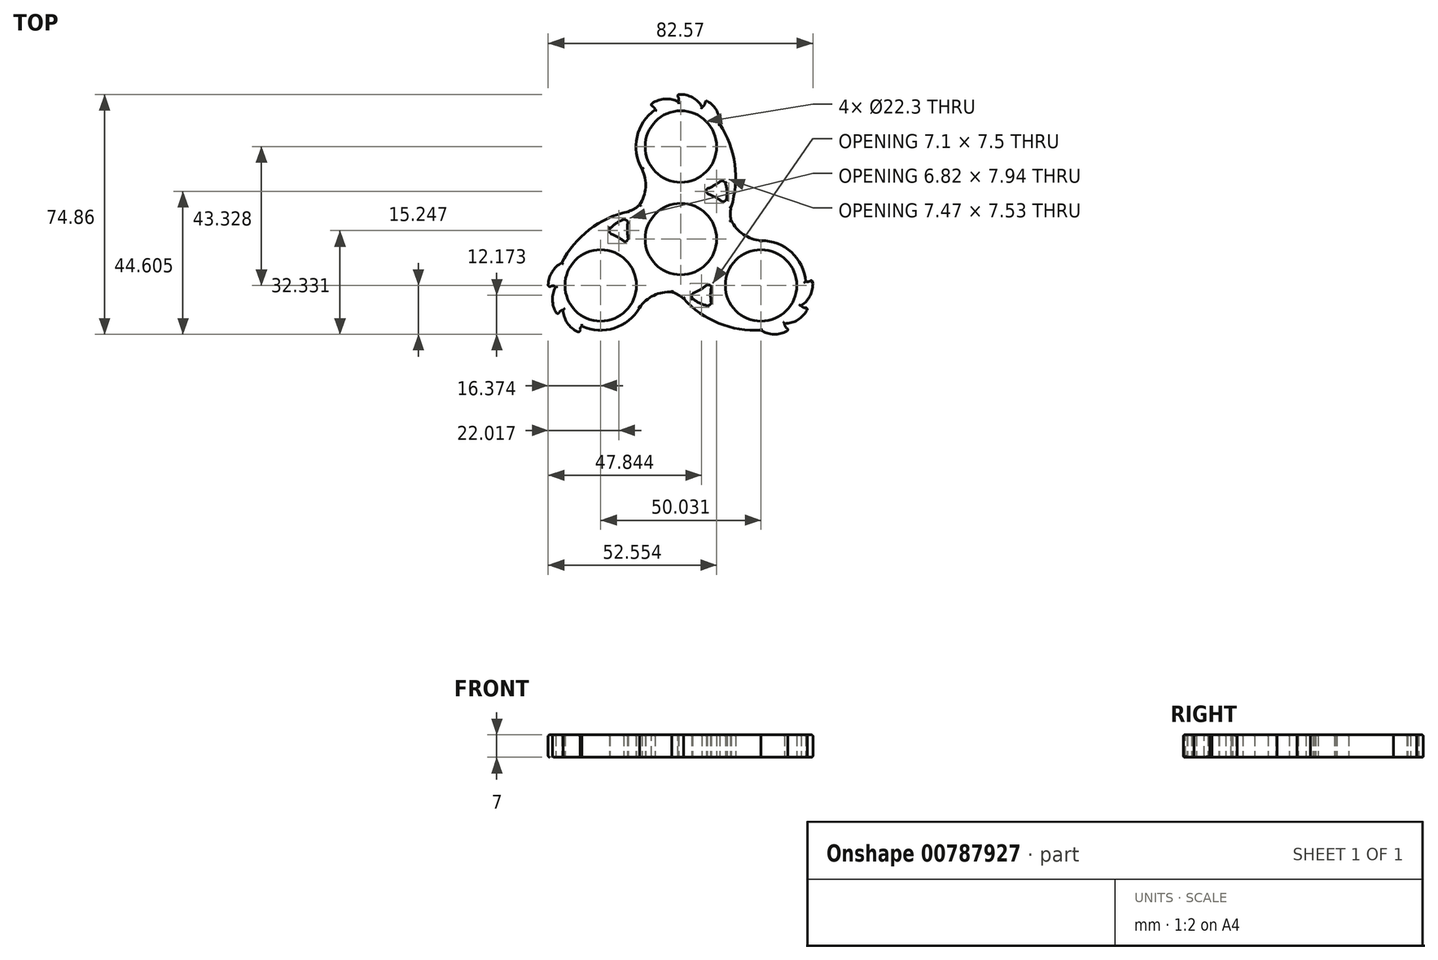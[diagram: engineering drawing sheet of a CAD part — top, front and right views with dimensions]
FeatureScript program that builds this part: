
annotation { "Feature Type Name" : "Feature", "Feature Type Description" : "" }
export const myFeature = defineFeature(function(context is Context, id is Id, definition is map)
    precondition{}
    {
        {
            var Q0;
            Q0=qCreatedBy(makeId("Top.planeOp"),FACE);
            var sketch = newSketch(context, id + "F0", { "sketchPlane" : qUnion([Q0])});
            skCircle(sketch, "E0", {"center": v(0, 28.89) * mm, "radius": 11.15 * mm});
            skCircle(sketch, "E1", {"center": v(0, 0) * mm, "radius": 14 * mm});
            skPoint(sketch, "E2.center", {"position": v(-0.02, -0.02) * mm});
            skPoint(sketch, "E3.1.3", {"position": v(0.02, 0) * mm});
            skPoint(sketch, "E3.2.3", {"position": v(0, 0.02) * mm});
            skArc(sketch, "E4", {"start": v(15.68, 10) * mm, "mid": v(16.82, 23.32) * mm, "end": v(12.15, 35.85) * mm});
            skArc(sketch, "E5", {"start": v(8.03, 15.65) * mm, "mid": v(7.97, 14.84) * mm, "end": v(8.4, 14.15) * mm});
            skArc(sketch, "E6", {"start": v(15.68, 10) * mm, "mid": v(15.44, 7.9) * mm, "end": v(15.68, 5.81) * mm});
            skArc(sketch, "E7", {"start": v(15.68, 5.81) * mm, "mid": v(19.88, 1.21) * mm, "end": v(25.87, -0.48) * mm});
            skArc(sketch, "E8", {"start": v(12.15, 35.85) * mm, "mid": v(10.91, 40.47) * mm, "end": v(7.24, 43.54) * mm});
            skArc(sketch, "E9", {"start": v(6.62, 41.22) * mm, "mid": v(7.48, 42.23) * mm, "end": v(7.24, 43.54) * mm});
            skArc(sketch, "E10", {"start": v(6.62, 41.22) * mm, "mid": v(3.06, 44.45) * mm, "end": v(-1.72, 45.02) * mm});
            skArc(sketch, "E11", {"start": v(-0.79, 42.86) * mm, "mid": v(-0.75, 44.16) * mm, "end": v(-1.72, 45.02) * mm});
            skArc(sketch, "E12", {"start": v(-0.79, 42.86) * mm, "mid": v(-5.54, 43.68) * mm, "end": v(-9.88, 41.6) * mm});
            skArc(sketch, "E13", {"start": v(-8.04, 40.35) * mm, "mid": v(-8.7, 41.36) * mm, "end": v(-9.88, 41.6) * mm});
            skArc(sketch, "E14", {"start": v(13.9, 17.47) * mm, "mid": v(13.31, 18.04) * mm, "end": v(12.5, 18.16) * mm});
            skArc(sketch, "E15", {"start": v(12.86, 11.66) * mm, "mid": v(13.65, 11.81) * mm, "end": v(14.21, 12.4) * mm});
            skArc(sketch, "E16", {"start": v(12.86, 11.66) * mm, "mid": v(10.72, 13.08) * mm, "end": v(8.4, 14.15) * mm});
            skArc(sketch, "E17", {"start": v(14.21, 12.4) * mm, "mid": v(14.38, 14.96) * mm, "end": v(13.9, 17.47) * mm});
            skArc(sketch, "E18", {"start": v(8.03, 15.65) * mm, "mid": v(10.38, 16.71) * mm, "end": v(12.5, 18.16) * mm});
            skArc(sketch, "E19.1.0", {"start": v(-12.88, 10.68) * mm, "mid": v(-10.99, 16.61) * mm, "end": v(-12.52, 22.64) * mm});
            skCircle(sketch, "E20", {"center": v(0, 0) * mm, "radius": 11.15 * mm});
            skCircle(sketch, "E21", {"center": v(0, 28.89) * mm, "radius": 14 * mm});
            skArc(sketch, "E22.1.0", {"start": v(-16.53, 5.3) * mm, "mid": v(-16.69, 2.75) * mm, "end": v(-16.45, 0.2) * mm});
            skArc(sketch, "E22.1.1", {"start": v(-17.85, 6.1) * mm, "mid": v(-20.15, 4.97) * mm, "end": v(-22.08, 3.3) * mm});
            skArc(sketch, "E22.1.2", {"start": v(-16.5, 8.59) * mm, "mid": v(-28.6, 2.9) * mm, "end": v(-37.12, -7.4) * mm});
            skArc(sketch, "E22.1.3", {"start": v(-37.12, -7.4) * mm, "mid": v(-40.5, -10.78) * mm, "end": v(-41.32, -15.5) * mm});
            skCircle(sketch, "E22.1.5", {"center": v(-25.02, -14.44) * mm, "radius": 11.15 * mm});
            skArc(sketch, "E22.1.7", {"start": v(-16.5, 8.59) * mm, "mid": v(-14.57, 9.42) * mm, "end": v(-12.88, 10.68) * mm});
            skArc(sketch, "E22.1.8", {"start": v(-39, -14.87) * mm, "mid": v(-40.03, -19.58) * mm, "end": v(-38.13, -24) * mm});
            skArc(sketch, "E22.1.9", {"start": v(-17.57, -0.87) * mm, "mid": v(-19.66, 0.63) * mm, "end": v(-21.98, 1.75) * mm});
            skCircle(sketch, "E22.1.10", {"center": v(-25.02, -14.44) * mm, "radius": 14 * mm});
            skArc(sketch, "E22.1.12", {"start": v(-36.73, -22.11) * mm, "mid": v(-35.06, -26.64) * mm, "end": v(-31.08, -29.36) * mm});
            skArc(sketch, "E22.1.13", {"start": v(-2.8, -16.49) * mm, "mid": v(-8.9, -17.82) * mm, "end": v(-13.35, -22.17) * mm});
            skArc(sketch, "E22.1.15", {"start": v(-30.92, -27.14) * mm, "mid": v(-31.48, -28.21) * mm, "end": v(-31.08, -29.36) * mm});
            skArc(sketch, "E22.1.18", {"start": v(-16.53, 5.3) * mm, "mid": v(-17.06, 5.92) * mm, "end": v(-17.85, 6.1) * mm});
            skArc(sketch, "E22.1.19", {"start": v(-39, -14.87) * mm, "mid": v(-40.31, -14.63) * mm, "end": v(-41.32, -15.5) * mm});
            skArc(sketch, "E22.1.20", {"start": v(-36.73, -22.11) * mm, "mid": v(-37.87, -22.73) * mm, "end": v(-38.13, -24) * mm});
            skArc(sketch, "E22.1.21", {"start": v(-17.57, -0.87) * mm, "mid": v(-16.84, -0.52) * mm, "end": v(-16.45, 0.2) * mm});
            skArc(sketch, "E22.1.22", {"start": v(-22.08, 3.3) * mm, "mid": v(-22.28, 2.5) * mm, "end": v(-21.98, 1.75) * mm});
            skArc(sketch, "E22.2.0", {"start": v(3.67, -16.96) * mm, "mid": v(5.97, -15.82) * mm, "end": v(8.06, -14.35) * mm});
            skArc(sketch, "E22.2.1", {"start": v(3.64, -18.5) * mm, "mid": v(5.77, -19.93) * mm, "end": v(8.19, -20.77) * mm});
            skArc(sketch, "E22.2.2", {"start": v(0.81, -18.58) * mm, "mid": v(11.78, -26.23) * mm, "end": v(24.97, -28.44) * mm});
            skArc(sketch, "E22.2.3", {"start": v(24.97, -28.44) * mm, "mid": v(29.59, -29.69) * mm, "end": v(34.08, -28.04) * mm});
            skCircle(sketch, "E22.2.5", {"center": v(25.02, -14.44) * mm, "radius": 11.15 * mm});
            skArc(sketch, "E22.2.6", {"start": v(-2.8, -16.49) * mm, "mid": v(-8.9, -17.82) * mm, "end": v(-13.35, -22.17) * mm});
            skArc(sketch, "E22.2.7", {"start": v(0.81, -18.58) * mm, "mid": v(-0.88, -17.33) * mm, "end": v(-2.8, -16.49) * mm});
            skArc(sketch, "E22.2.8", {"start": v(32.39, -26.35) * mm, "mid": v(36.97, -24.88) * mm, "end": v(39.85, -21.02) * mm});
            skArc(sketch, "E22.2.9", {"start": v(9.54, -14.78) * mm, "mid": v(9.29, -17.34) * mm, "end": v(9.47, -19.91) * mm});
            skCircle(sketch, "E22.2.10", {"center": v(25.02, -14.44) * mm, "radius": 14 * mm});
            skArc(sketch, "E22.2.12", {"start": v(37.51, -20.75) * mm, "mid": v(40.6, -17.05) * mm, "end": v(40.96, -12.24) * mm});
            skArc(sketch, "E22.2.15", {"start": v(38.96, -13.21) * mm, "mid": v(40.17, -13.15) * mm, "end": v(40.96, -12.24) * mm});
            skArc(sketch, "E22.2.18", {"start": v(3.67, -16.96) * mm, "mid": v(3.4, -17.73) * mm, "end": v(3.64, -18.5) * mm});
            skArc(sketch, "E22.2.19", {"start": v(32.39, -26.35) * mm, "mid": v(32.83, -27.6) * mm, "end": v(34.08, -28.04) * mm});
            skArc(sketch, "E22.2.20", {"start": v(37.51, -20.75) * mm, "mid": v(38.62, -21.43) * mm, "end": v(39.85, -21.02) * mm});
            skArc(sketch, "E22.2.21", {"start": v(9.54, -14.78) * mm, "mid": v(8.87, -14.32) * mm, "end": v(8.06, -14.35) * mm});
            skArc(sketch, "E22.2.22", {"start": v(8.19, -20.77) * mm, "mid": v(8.97, -20.55) * mm, "end": v(9.47, -19.91) * mm});
            skSolve(sketch);
        }
        {
            var Q0;
            {var subQ12=sQuery(id+"F0.wireOp",EDGE,"E4");Q0=makeQuery(id+"F0.imprint","IMPRINT",FACE,{"disambiguationData":[TD([[makeQuery(id+"F0.imprint","IMPRINT",EDGE,{"derivedFrom":subQ12}),1.0]])]});}
            var Q1;
            Q1=makeQuery(id+"F0.imprint","IMPRINT",FACE,{"disambiguationData":[TD([[makeQuery(id+"F0.imprint","IMPRINT",EDGE,{"derivedFrom":sQuery(id+"F0.wireOp",EDGE,"E0")}),-1.0]])]});
            var Q2;
            Q2=makeQuery(id+"F0.imprint","IMPRINT",FACE,{"disambiguationData":[TD([[makeQuery(id+"F0.imprint","IMPRINT",EDGE,{"derivedFrom":sQuery(id+"F0.wireOp",EDGE,"E22.1.5")}),-1.0]])]});
            var Q3;
            Q3=makeQuery(id+"F0.imprint","IMPRINT",FACE,{"disambiguationData":[TD([[makeQuery(id+"F0.imprint","IMPRINT",EDGE,{"derivedFrom":sQuery(id+"F0.wireOp",EDGE,"E22.2.5")}),-1.0]])]});
            var Q4;
            Q4=makeQuery(id+"F0.imprint","IMPRINT",FACE,{"disambiguationData":[TD([[makeQuery(id+"F0.imprint","IMPRINT",EDGE,{"derivedFrom":sQuery(id+"F0.wireOp",EDGE,"E1")}),1.0]])]});
            var Q5;
            {var subQ0=sQuery(id+"F0.wireOp",EDGE,"E12");Q5=makeQuery(id+"F0.imprint","IMPRINT",FACE,{"disambiguationData":[TD([[makeQuery(id+"F0.imprint","IMPRINT",EDGE,{"derivedFrom":subQ0}),1.0]])]});}
            var Q6;
            {var subQ0=sQuery(id+"F0.wireOp",EDGE,"E10");Q6=makeQuery(id+"F0.imprint","IMPRINT",FACE,{"disambiguationData":[TD([[makeQuery(id+"F0.imprint","IMPRINT",EDGE,{"derivedFrom":subQ0}),1.0]])]});}
            var Q7;
            {var subQ0=sQuery(id+"F0.wireOp",EDGE,"E8");Q7=makeQuery(id+"F0.imprint","IMPRINT",FACE,{"disambiguationData":[TD([[makeQuery(id+"F0.imprint","IMPRINT",EDGE,{"derivedFrom":subQ0}),1.0]])]});}
            var Q8;
            {var subQ0=sQuery(id+"F0.wireOp",EDGE,"E22.2.12");Q8=makeQuery(id+"F0.imprint","IMPRINT",FACE,{"disambiguationData":[TD([[makeQuery(id+"F0.imprint","IMPRINT",EDGE,{"derivedFrom":subQ0}),1.0]])]});}
            var Q9;
            {var subQ0=sQuery(id+"F0.wireOp",EDGE,"E22.2.8");Q9=makeQuery(id+"F0.imprint","IMPRINT",FACE,{"disambiguationData":[TD([[makeQuery(id+"F0.imprint","IMPRINT",EDGE,{"derivedFrom":subQ0}),1.0]])]});}
            var Q10;
            {var subQ0=sQuery(id+"F0.wireOp",EDGE,"E22.2.3");Q10=makeQuery(id+"F0.imprint","IMPRINT",FACE,{"disambiguationData":[TD([[makeQuery(id+"F0.imprint","IMPRINT",EDGE,{"derivedFrom":subQ0}),1.0]])]});}
            var Q11;
            {var subQ0=sQuery(id+"F0.wireOp",EDGE,"E22.1.12");Q11=makeQuery(id+"F0.imprint","IMPRINT",FACE,{"disambiguationData":[TD([[makeQuery(id+"F0.imprint","IMPRINT",EDGE,{"derivedFrom":subQ0}),1.0]])]});}
            var Q12;
            {var subQ0=sQuery(id+"F0.wireOp",EDGE,"E22.1.8");Q12=makeQuery(id+"F0.imprint","IMPRINT",FACE,{"disambiguationData":[TD([[makeQuery(id+"F0.imprint","IMPRINT",EDGE,{"derivedFrom":subQ0}),1.0]])]});}
            var Q13;
            {var subQ0=sQuery(id+"F0.wireOp",EDGE,"E22.1.3");Q13=makeQuery(id+"F0.imprint","IMPRINT",FACE,{"disambiguationData":[TD([[makeQuery(id+"F0.imprint","IMPRINT",EDGE,{"derivedFrom":subQ0}),1.0]])]});}
            extrude(context, id + "F1", {"entities" : qUnion([Q0, Q1, Q2, Q3, Q4, Q5, Q6, Q7, Q8, Q9, Q10, Q11, Q12, Q13]), "depth" : 7 * mm, "offsetDistance" : 25 * mm});
        }
        {
            var Q0;
            Q0=makeQuery(id+"F1.opExtrude","CAP_FACE",FACE,{"disambiguationData":[OSD([sQuery(id+"F0.wireOp",EDGE,"E0"),sQuery(id+"F0.wireOp",EDGE,"E4"),sQuery(id+"F0.wireOp",EDGE,"E5"),sQuery(id+"F0.wireOp",EDGE,"E6"),sQuery(id+"F0.wireOp",EDGE,"E8"),sQuery(id+"F0.wireOp",EDGE,"E9"),sQuery(id+"F0.wireOp",EDGE,"E10"),sQuery(id+"F0.wireOp",EDGE,"E11"),sQuery(id+"F0.wireOp",EDGE,"E12"),sQuery(id+"F0.wireOp",EDGE,"E13"),sQuery(id+"F0.wireOp",EDGE,"E14"),sQuery(id+"F0.wireOp",EDGE,"E15"),sQuery(id+"F0.wireOp",EDGE,"E16"),sQuery(id+"F0.wireOp",EDGE,"E17"),sQuery(id+"F0.wireOp",EDGE,"E18"),sQuery(id+"F0.wireOp",EDGE,"E21"),sQuery(id+"F0.wireOp",EDGE,"E22.1.0"),sQuery(id+"F0.wireOp",EDGE,"E22.1.1"),sQuery(id+"F0.wireOp",EDGE,"E22.1.2"),sQuery(id+"F0.wireOp",EDGE,"E22.1.3"),sQuery(id+"F0.wireOp",EDGE,"E22.1.5"),sQuery(id+"F0.wireOp",EDGE,"E19.1.0"),sQuery(id+"F0.wireOp",EDGE,"E22.1.7"),sQuery(id+"F0.wireOp",EDGE,"E22.1.8"),sQuery(id+"F0.wireOp",EDGE,"E22.1.9"),sQuery(id+"F0.wireOp",EDGE,"E22.1.10"),sQuery(id+"F0.wireOp",EDGE,"E22.1.12"),sQuery(id+"F0.wireOp",EDGE,"E22.1.15"),sQuery(id+"F0.wireOp",EDGE,"E22.1.18"),sQuery(id+"F0.wireOp",EDGE,"E22.1.19"),sQuery(id+"F0.wireOp",EDGE,"E22.1.20"),sQuery(id+"F0.wireOp",EDGE,"E22.1.21"),sQuery(id+"F0.wireOp",EDGE,"E22.1.22"),sQuery(id+"F0.wireOp",EDGE,"E22.2.0"),sQuery(id+"F0.wireOp",EDGE,"E22.2.1"),sQuery(id+"F0.wireOp",EDGE,"E22.2.2"),sQuery(id+"F0.wireOp",EDGE,"E22.2.3"),sQuery(id+"F0.wireOp",EDGE,"E22.2.5"),sQuery(id+"F0.wireOp",EDGE,"E22.2.6"),sQuery(id+"F0.wireOp",EDGE,"E22.2.7"),sQuery(id+"F0.wireOp",EDGE,"E22.2.8"),sQuery(id+"F0.wireOp",EDGE,"E22.2.9"),sQuery(id+"F0.wireOp",EDGE,"E22.2.10"),sQuery(id+"F0.wireOp",EDGE,"E22.2.12"),sQuery(id+"F0.wireOp",EDGE,"E7"),sQuery(id+"F0.wireOp",EDGE,"E20"),sQuery(id+"F0.wireOp",EDGE,"E22.2.15"),sQuery(id+"F0.wireOp",EDGE,"E22.2.18"),sQuery(id+"F0.wireOp",EDGE,"E22.2.19"),sQuery(id+"F0.wireOp",EDGE,"E22.2.20"),sQuery(id+"F0.wireOp",EDGE,"E22.2.21"),sQuery(id+"F0.wireOp",EDGE,"E22.2.22")])],"isStart":false});
            var Q1;
            Q1=makeQuery(id+"F1.opExtrude","CAP_FACE",FACE,{"disambiguationData":[OSD([sQuery(id+"F0.wireOp",EDGE,"E0"),sQuery(id+"F0.wireOp",EDGE,"E4"),sQuery(id+"F0.wireOp",EDGE,"E5"),sQuery(id+"F0.wireOp",EDGE,"E6"),sQuery(id+"F0.wireOp",EDGE,"E8"),sQuery(id+"F0.wireOp",EDGE,"E9"),sQuery(id+"F0.wireOp",EDGE,"E10"),sQuery(id+"F0.wireOp",EDGE,"E11"),sQuery(id+"F0.wireOp",EDGE,"E12"),sQuery(id+"F0.wireOp",EDGE,"E13"),sQuery(id+"F0.wireOp",EDGE,"E14"),sQuery(id+"F0.wireOp",EDGE,"E15"),sQuery(id+"F0.wireOp",EDGE,"E16"),sQuery(id+"F0.wireOp",EDGE,"E17"),sQuery(id+"F0.wireOp",EDGE,"E18"),sQuery(id+"F0.wireOp",EDGE,"E21"),sQuery(id+"F0.wireOp",EDGE,"E22.1.0"),sQuery(id+"F0.wireOp",EDGE,"E22.1.1"),sQuery(id+"F0.wireOp",EDGE,"E22.1.2"),sQuery(id+"F0.wireOp",EDGE,"E22.1.3"),sQuery(id+"F0.wireOp",EDGE,"E22.1.5"),sQuery(id+"F0.wireOp",EDGE,"E19.1.0"),sQuery(id+"F0.wireOp",EDGE,"E22.1.7"),sQuery(id+"F0.wireOp",EDGE,"E22.1.8"),sQuery(id+"F0.wireOp",EDGE,"E22.1.9"),sQuery(id+"F0.wireOp",EDGE,"E22.1.10"),sQuery(id+"F0.wireOp",EDGE,"E22.1.12"),sQuery(id+"F0.wireOp",EDGE,"E22.1.15"),sQuery(id+"F0.wireOp",EDGE,"E22.1.18"),sQuery(id+"F0.wireOp",EDGE,"E22.1.19"),sQuery(id+"F0.wireOp",EDGE,"E22.1.20"),sQuery(id+"F0.wireOp",EDGE,"E22.1.21"),sQuery(id+"F0.wireOp",EDGE,"E22.1.22"),sQuery(id+"F0.wireOp",EDGE,"E22.2.0"),sQuery(id+"F0.wireOp",EDGE,"E22.2.1"),sQuery(id+"F0.wireOp",EDGE,"E22.2.2"),sQuery(id+"F0.wireOp",EDGE,"E22.2.3"),sQuery(id+"F0.wireOp",EDGE,"E22.2.5"),sQuery(id+"F0.wireOp",EDGE,"E22.2.6"),sQuery(id+"F0.wireOp",EDGE,"E22.2.7"),sQuery(id+"F0.wireOp",EDGE,"E22.2.8"),sQuery(id+"F0.wireOp",EDGE,"E22.2.9"),sQuery(id+"F0.wireOp",EDGE,"E22.2.10"),sQuery(id+"F0.wireOp",EDGE,"E22.2.12"),sQuery(id+"F0.wireOp",EDGE,"E7"),sQuery(id+"F0.wireOp",EDGE,"E20"),sQuery(id+"F0.wireOp",EDGE,"E22.2.15"),sQuery(id+"F0.wireOp",EDGE,"E22.2.18"),sQuery(id+"F0.wireOp",EDGE,"E22.2.19"),sQuery(id+"F0.wireOp",EDGE,"E22.2.20"),sQuery(id+"F0.wireOp",EDGE,"E22.2.21"),sQuery(id+"F0.wireOp",EDGE,"E22.2.22")])],"isStart":true});
            var Q2;
            Q2=makeQuery(id+"F1.opExtrude","SWEPT_EDGE",EDGE,{"disambiguationData":[OSD([sQuery(id+"F0.wireOp",EDGE,"E12"),sQuery(id+"F0.wireOp",EDGE,"E13")])]});
            var Q3;
            Q3=makeQuery(id+"F1.opExtrude","SWEPT_EDGE",EDGE,{"disambiguationData":[OSD([sQuery(id+"F0.wireOp",EDGE,"E10"),sQuery(id+"F0.wireOp",EDGE,"E11")])]});
            var Q4;
            Q4=makeQuery(id+"F1.opExtrude","SWEPT_EDGE",EDGE,{"disambiguationData":[OSD([sQuery(id+"F0.wireOp",EDGE,"E8"),sQuery(id+"F0.wireOp",EDGE,"E9")])]});
            var Q5;
            Q5=makeQuery(id+"F1.opExtrude","SWEPT_EDGE",EDGE,{"disambiguationData":[OSD([sQuery(id+"F0.wireOp",EDGE,"E22.1.3"),sQuery(id+"F0.wireOp",EDGE,"E22.1.19")])]});
            var Q6;
            Q6=makeQuery(id+"F1.opExtrude","SWEPT_EDGE",EDGE,{"disambiguationData":[OSD([sQuery(id+"F0.wireOp",EDGE,"E22.1.8"),sQuery(id+"F0.wireOp",EDGE,"E22.1.20")])]});
            var Q7;
            Q7=makeQuery(id+"F1.opExtrude","SWEPT_EDGE",EDGE,{"disambiguationData":[OSD([sQuery(id+"F0.wireOp",EDGE,"E22.1.12"),sQuery(id+"F0.wireOp",EDGE,"E22.1.15")])]});
            var Q8;
            Q8=makeQuery(id+"F1.opExtrude","SWEPT_EDGE",EDGE,{"disambiguationData":[OSD([sQuery(id+"F0.wireOp",EDGE,"E22.2.3"),sQuery(id+"F0.wireOp",EDGE,"E22.2.19")])]});
            var Q9;
            Q9=makeQuery(id+"F1.opExtrude","SWEPT_EDGE",EDGE,{"disambiguationData":[OSD([sQuery(id+"F0.wireOp",EDGE,"E22.2.8"),sQuery(id+"F0.wireOp",EDGE,"E22.2.20")])]});
            var Q10;
            Q10=makeQuery(id+"F1.opExtrude","SWEPT_EDGE",EDGE,{"disambiguationData":[OSD([sQuery(id+"F0.wireOp",EDGE,"E22.2.12"),sQuery(id+"F0.wireOp",EDGE,"E22.2.15")])]});
            var Q11;
            Q11=makeQuery(id+"F1.opExtrude","SWEPT_EDGE",EDGE,{"disambiguationData":[OSD([sQuery(id+"F0.wireOp",EDGE,"E22.1.9"),sQuery(id+"F0.wireOp",EDGE,"E22.1.22")])]});
            var Q12;
            Q12=makeQuery(id+"F1.opExtrude","SWEPT_EDGE",EDGE,{"disambiguationData":[OSD([sQuery(id+"F0.wireOp",EDGE,"E22.1.9"),sQuery(id+"F0.wireOp",EDGE,"E22.1.21")])]});
            var Q13;
            Q13=makeQuery(id+"F1.opExtrude","SWEPT_EDGE",EDGE,{"disambiguationData":[OSD([sQuery(id+"F0.wireOp",EDGE,"E22.1.0"),sQuery(id+"F0.wireOp",EDGE,"E22.1.21")])]});
            var Q14;
            Q14=makeQuery(id+"F1.opExtrude","SWEPT_EDGE",EDGE,{"disambiguationData":[OSD([sQuery(id+"F0.wireOp",EDGE,"E22.1.0"),sQuery(id+"F0.wireOp",EDGE,"E22.1.18")])]});
            var Q15;
            Q15=makeQuery(id+"F1.opExtrude","SWEPT_EDGE",EDGE,{"disambiguationData":[OSD([sQuery(id+"F0.wireOp",EDGE,"E22.2.0"),sQuery(id+"F0.wireOp",EDGE,"E22.2.18")])]});
            var Q16;
            Q16=makeQuery(id+"F1.opExtrude","SWEPT_FACE",FACE,{"disambiguationData":[OSD([sQuery(id+"F0.wireOp",EDGE,"E22.2.0")])]});
            var Q17;
            Q17=makeQuery(id+"F1.opExtrude","SWEPT_EDGE",EDGE,{"disambiguationData":[OSD([sQuery(id+"F0.wireOp",EDGE,"E22.2.9"),sQuery(id+"F0.wireOp",EDGE,"E22.2.21")])]});
            var Q18;
            Q18=makeQuery(id+"F1.opExtrude","SWEPT_EDGE",EDGE,{"disambiguationData":[OSD([sQuery(id+"F0.wireOp",EDGE,"E22.2.9"),sQuery(id+"F0.wireOp",EDGE,"E22.2.22")])]});
            var Q19;
            Q19=makeQuery(id+"F1.opExtrude","SWEPT_EDGE",EDGE,{"disambiguationData":[OSD([sQuery(id+"F0.wireOp",EDGE,"E5"),sQuery(id+"F0.wireOp",EDGE,"E16")])]});
            var Q20;
            Q20=makeQuery(id+"F1.opExtrude","SWEPT_EDGE",EDGE,{"disambiguationData":[OSD([sQuery(id+"F0.wireOp",EDGE,"E5"),sQuery(id+"F0.wireOp",EDGE,"E18")])]});
            var Q21;
            Q21=makeQuery(id+"F1.opExtrude","SWEPT_EDGE",EDGE,{"disambiguationData":[OSD([sQuery(id+"F0.wireOp",EDGE,"E15"),sQuery(id+"F0.wireOp",EDGE,"E16")])]});
            var Q22;
            Q22=makeQuery(id+"F1.opExtrude","SWEPT_EDGE",EDGE,{"disambiguationData":[OSD([sQuery(id+"F0.wireOp",EDGE,"E14"),sQuery(id+"F0.wireOp",EDGE,"E18")])]});
            fillet(context, id + "F2", {"entities" : qUnion([Q0, Q1, Q2, Q3, Q4, Q5, Q6, Q7, Q8, Q9, Q10, Q11, Q12, Q13, Q14, Q15, Q16, Q17, Q18, Q19, Q20, Q21, Q22]), "radius" : .5 * mm, "tangentPropagation" : true, "allowEdgeOverflow" : false});
        }
    });
